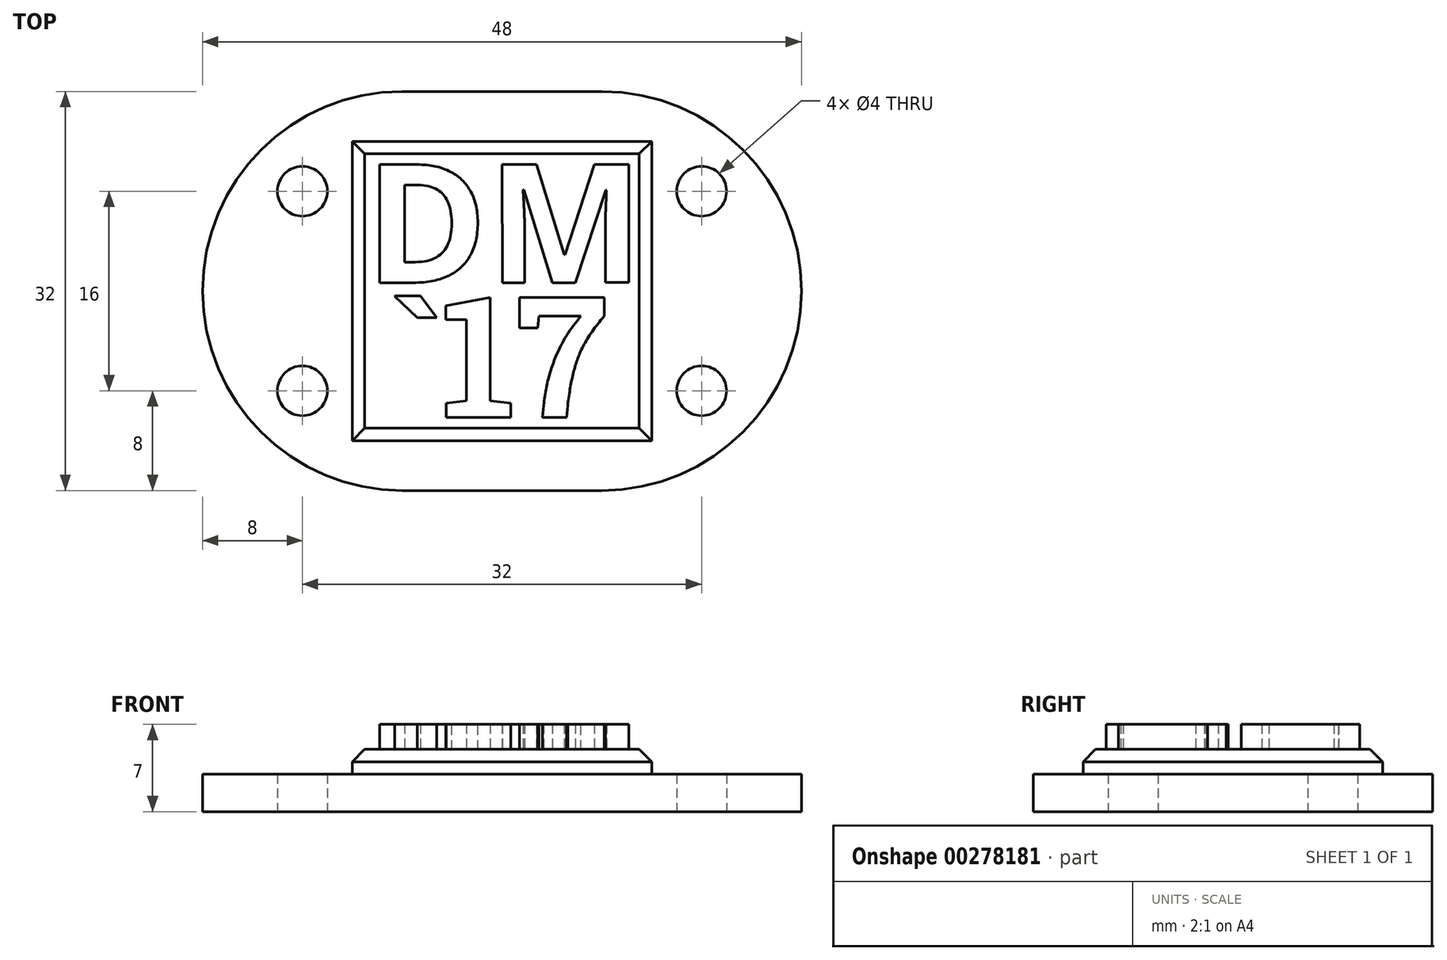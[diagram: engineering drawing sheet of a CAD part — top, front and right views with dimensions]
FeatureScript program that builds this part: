
annotation { "Feature Type Name" : "Feature", "Feature Type Description" : "" }
export const myFeature = defineFeature(function(context is Context, id is Id, definition is map)
    precondition{}
    {
        {
            var Q0;
            Q0=qCreatedBy(makeId("Top.planeOp"),FACE);
            var sketch = newSketch(context, id + "F0", { "sketchPlane" : qUnion([Q0])});
            skLineSegment(sketch, "E0.bottom", {"start": v(-24, 16) * mm, "end": v(24, 16) * mm});
            skLineSegment(sketch, "E0.top", {"start": v(-24, -16) * mm, "end": v(24, -16) * mm});
            skLineSegment(sketch, "E0.left", {"start": v(-24, 16) * mm, "end": v(-24, -16) * mm});
            skLineSegment(sketch, "E0.right", {"start": v(24, 16) * mm, "end": v(24, -16) * mm});
            skPoint(sketch, "E0.middle", {"position": v(0, 0) * mm});
            skLineSegment(sketch, "E1", {"start": v(0, 0) * mm, "end": v(-8, 0) * mm});
            skLineSegment(sketch, "E2", {"start": v(-8, 0) * mm, "end": v(-16, 0) * mm});
            skLineSegment(sketch, "E3", {"start": v(-16, 0) * mm, "end": v(-16, 8) * mm});
            skLineSegment(sketch, "E4", {"start": v(0, 0) * mm, "end": v(8, 0) * mm});
            skLineSegment(sketch, "E5", {"start": v(8, 0) * mm, "end": v(16, 0) * mm});
            skLineSegment(sketch, "E6", {"start": v(16, 0) * mm, "end": v(16, 8) * mm});
            skLineSegment(sketch, "E7", {"start": v(16, 0) * mm, "end": v(16, -8) * mm});
            skLineSegment(sketch, "E8", {"start": v(-16, 0) * mm, "end": v(-16, -8) * mm});
            skCircle(sketch, "E9", {"center": v(-16, 8) * mm, "radius": 2 * mm});
            skCircle(sketch, "E10", {"center": v(16, 8) * mm, "radius": 2 * mm});
            skCircle(sketch, "E11", {"center": v(16, -8) * mm, "radius": 2 * mm});
            skCircle(sketch, "E12", {"center": v(-16, -8) * mm, "radius": 2 * mm});
            skArc(sketch, "E13", {"start": v(-8, 16) * mm, "mid": v(-24, 0) * mm, "end": v(-8, -16) * mm});
            skArc(sketch, "E14", {"start": v(8, -16) * mm, "mid": v(24, 0) * mm, "end": v(8, 16) * mm});
            skLineSegment(sketch, "E15", {"start": v(24, -16) * mm, "end": v(8, -16) * mm});
            skLineSegment(sketch, "E16", {"start": v(24, 16) * mm, "end": v(8, 16) * mm});
            skLineSegment(sketch, "E17", {"start": v(-8, 16) * mm, "end": v(-24, 16) * mm});
            skLineSegment(sketch, "E18", {"start": v(-8, -16) * mm, "end": v(-24, -16) * mm});
            skSolve(sketch);
        }
        {
            var Q0;
            Q0=makeQuery(id+"F0.imprint","IMPRINT",FACE,{"disambiguationData":[TD([[makeQuery(id+"F0.imprint","IMPRINT",EDGE,{"derivedFrom":sQuery(id+"F0.wireOp",EDGE,"E9")}),-1.0]])]});
            var Q1;
            {var subQ7=sQuery(id+"F0.wireOp",EDGE,"E14");var subQ8=sQuery(id+"F0.wireOp",EDGE,"E0.right");var subQ9=makeQuery(id+"F0.imprint","INTERSECT",VERTEX,{"disambiguationData":[OD(0.0)],"derivedFrom":[subQ8,subQ7]});Q1=makeQuery(id+"F0.imprint","IMPRINT",FACE,{"disambiguationData":[TD([[makeQuery(id+"F0.imprint","IMPRINT",EDGE,{"disambiguationData":[TD([[subQ9,-1.0]])],"derivedFrom":subQ8}),1.0]])]});}
            var Q2;
            Q2=makeQuery(id+"F0.imprint","IMPRINT",FACE,{"disambiguationData":[TD([[makeQuery(id+"F0.imprint","IMPRINT",EDGE,{"derivedFrom":sQuery(id+"F0.wireOp",EDGE,"E1")}),1.0]])]});
            var Q3;
            Q3=makeQuery(id+"F0.imprint","IMPRINT",FACE,{"disambiguationData":[TD([[makeQuery(id+"F0.imprint","IMPRINT",EDGE,{"derivedFrom":sQuery(id+"F0.wireOp",EDGE,"E1")}),-1.0]])]});
            extrude(context, id + "F1", {"entities" : qUnion([Q0, Q1, Q2, Q3]), "depth" : 3 * mm});
        }
        {
            var Q0;
            Q0=makeQuery(id+"F1.opExtrude","CAP_FACE",FACE,{"disambiguationData":[OSD([sQuery(id+"F0.wireOp",EDGE,"E0.bottom"),sQuery(id+"F0.wireOp",EDGE,"E0.top"),sQuery(id+"F0.wireOp",EDGE,"E9"),sQuery(id+"F0.wireOp",EDGE,"E10"),sQuery(id+"F0.wireOp",EDGE,"E11"),sQuery(id+"F0.wireOp",EDGE,"E12"),sQuery(id+"F0.wireOp",EDGE,"E13"),sQuery(id+"F0.wireOp",EDGE,"E14")])],"isStart":false});
            var sketch = newSketch(context, id + "F2", { "sketchPlane" : qUnion([Q0])});
            skPoint(sketch, "E19", {"position": v(3.88, -14.56) * mm});
            skPoint(sketch, "E20", {"position": v(0, 16) * mm});
            skLineSegment(sketch, "E21", {"start": v(16, -8) * mm, "end": v(8, -16) * mm});
            skLineSegment(sketch, "E22", {"start": v(8, -16) * mm, "end": v(12, -12) * mm});
            skLineSegment(sketch, "E23", {"start": v(-16, 8) * mm, "end": v(-8, 16) * mm});
            skLineSegment(sketch, "E24.bottom", {"start": v(12, -12) * mm, "end": v(-12, -12) * mm});
            skLineSegment(sketch, "E24.top", {"start": v(12, 12) * mm, "end": v(-12, 12) * mm});
            skLineSegment(sketch, "E24.left", {"start": v(12, -12) * mm, "end": v(12, 12) * mm});
            skLineSegment(sketch, "E24.right", {"start": v(-12, -12) * mm, "end": v(-12, 12) * mm});
            skSolve(sketch);
        }
        {
            var Q0;
            Q0 = qSketchRegion(id + "F2", true);
            extrude(context, id + "F3", {"entities" : qUnion([Q0]), "operationType" : NewBodyOperationType.ADD, "depth" : 2 * mm});
        }
        {
            var Q0;
            Q0=makeQuery(id+"F3.opExtrude","CAP_EDGE",EDGE,{"disambiguationData":[OSD([sQuery(id+"F2.wireOp",EDGE,"E24.bottom")])],"isStart":false});
            var Q1;
            Q1=makeQuery(id+"F3.opExtrude","CAP_EDGE",EDGE,{"disambiguationData":[OSD([sQuery(id+"F2.wireOp",EDGE,"E24.left")])],"isStart":false});
            var Q2;
            Q2=makeQuery(id+"F3.opExtrude","CAP_EDGE",EDGE,{"disambiguationData":[OSD([sQuery(id+"F2.wireOp",EDGE,"E24.top")])],"isStart":false});
            var Q3;
            Q3=makeQuery(id+"F3.opExtrude","CAP_EDGE",EDGE,{"disambiguationData":[OSD([sQuery(id+"F2.wireOp",EDGE,"E24.right")])],"isStart":false});
            chamfer(context, id + "F4", {"entities" : qUnion([Q0, Q1, Q2, Q3]), "width" : 1 * mm, "tangentPropagation" : true});
        }
        {
            var Q0;
            Q0=makeQuery(id+"F3.opExtrude","CAP_FACE",FACE,{"disambiguationData":[OSD([sQuery(id+"F2.wireOp",EDGE,"E24.bottom"),sQuery(id+"F2.wireOp",EDGE,"E24.top"),sQuery(id+"F2.wireOp",EDGE,"E24.left"),sQuery(id+"F2.wireOp",EDGE,"E24.right")])],"isStart":false});
            var sketch = newSketch(context, id + "F5", { "sketchPlane" : qUnion([Q0])});
            skText(sketch, "E25", { "text": "DM", "fontName": "OpenSans-Bold.ttf"});
            skText(sketch, "E26", { "text": "`17", "fontName": "RobotoSlab-Bold.ttf"});
            const initialGuessF5  = {"E25": [-0.011, 0.00066, 1, 0.00067, 0.00956], "E26": [-0.00902, -0.01015, 1, 0, 0.00974]};
            skSetInitialGuess(sketch, initialGuessF5);
            skSolve(sketch);
        }
        {
            var Q0;
            Q0 = qSketchRegion(id + "F5", true);
            extrude(context, id + "F6", {"entities" : qUnion([Q0]), "operationType" : NewBodyOperationType.ADD, "depth" : 2 * mm});
        }
    });
